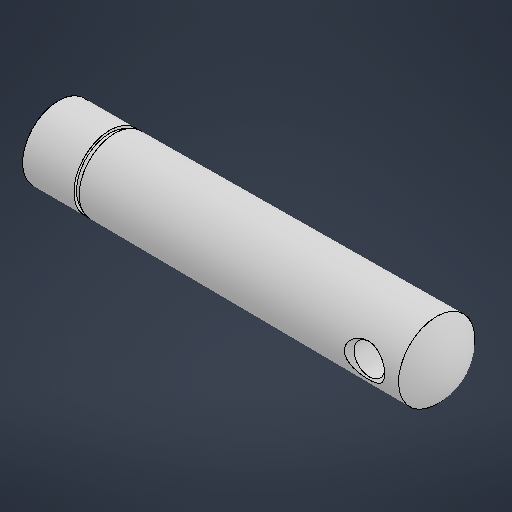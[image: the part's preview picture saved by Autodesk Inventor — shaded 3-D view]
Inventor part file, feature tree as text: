
AUTODESK INVENTOR PART (.ipt)
format: ipt  version: 2025.3 (Build 293356000, 356)  size: 244,224 bytes
history: native  units: mm
features: sketch x2, revolve x2, extrude x1, mirror x1
ambient origin geometry x8: Origin, YZ Plane, XZ Plane, XY Plane, X Axis, Y Axis, Z Axis, Center Point
bodies: Solid1 (feature_tree)
feature tree (6):
  sketch  "Sketch1"  dims[d4=0.066323mm d5=10.2mm]
  revolve  "Revolution1"  [1 undecoded]
  extrude  "Extrusion1"  Depth=10.0mm
  revolve  "Revolution2"  [1 undecoded]
  mirror  "Mirror1"
  sketch  "Sketch2"  dims[d6=14.0mm d7=14.0mm d11=50.0mm d13=60.0deg d19=10.0mm d20=77.0mm d21=67.0mm d22=6.0mm d23=0.5mm d24=10.0mm d25=1.0mm d26=90.0deg d27=0.0mm d28=0.0mm d29=45.0deg d30=1.0mm d31=90.0deg d32=14.83181mm]
note: 2 required parameter values undecoded (feature->parameter linkage not recoverable at this tier; creation-order binding heuristic only, values carry confidence <= 0.55)
